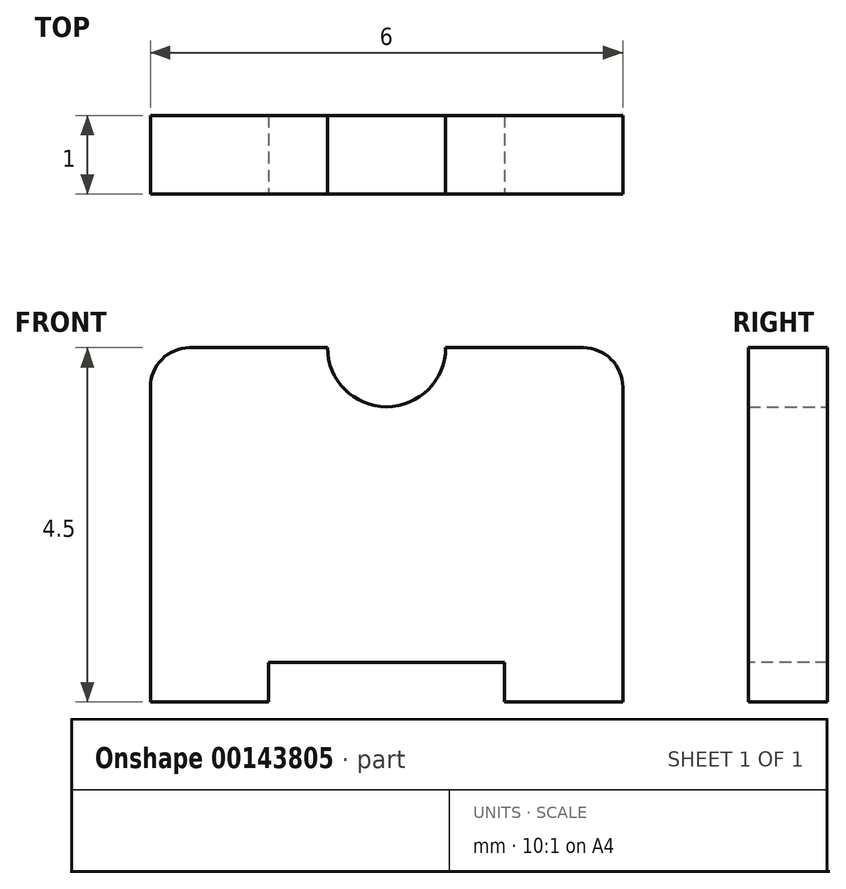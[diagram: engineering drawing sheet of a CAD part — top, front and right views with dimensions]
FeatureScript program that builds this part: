
annotation { "Feature Type Name" : "Feature", "Feature Type Description" : "" }
export const myFeature = defineFeature(function(context is Context, id is Id, definition is map)
    precondition{}
    {
        {
            var Q0;
            Q0=qCreatedBy(makeId("Front.planeOp"),FACE);
            var sketch = newSketch(context, id + "F0", { "sketchPlane" : qUnion([Q0])});
            skArc(sketch, "E0", {"start": v(-0.75, 0) * mm, "mid": v(0, -0.75) * mm, "end": v(0.75, 0) * mm});
            skLineSegment(sketch, "E1", {"start": v(-0.75, 0) * mm, "end": v(-2.5, 0) * mm});
            skLineSegment(sketch, "E2", {"start": v(-3, -0.5) * mm, "end": v(-3, -4.5) * mm});
            skLineSegment(sketch, "E3", {"start": v(-3, -4.5) * mm, "end": v(3, -4.5) * mm});
            skLineSegment(sketch, "E4", {"start": v(3, -4.5) * mm, "end": v(3, -0.5) * mm});
            skLineSegment(sketch, "E5", {"start": v(2.5, 0) * mm, "end": v(0.75, 0) * mm});
            skPoint(sketch, "E6.visualSharp", {"position": v(-3, 0) * mm});
            skArc(sketch, "E6.filletArc", {"start": v(-2.5, 0) * mm, "mid": v(-2.85, -0.15) * mm, "end": v(-3, -0.5) * mm});
            skPoint(sketch, "E7.visualSharp", {"position": v(3, 0) * mm});
            skArc(sketch, "E7.filletArc", {"start": v(3, -0.5) * mm, "mid": v(2.85, -0.15) * mm, "end": v(2.5, 0) * mm});
            skSolve(sketch);
        }
        {
            var Q0;
            Q0 = qSketchRegion(id + "F0", true);
            extrude(context, id + "F1", {"entities" : qUnion([Q0]), "depth" : 1 * mm});
        }
        {
            var Q0;
            Q0=makeQuery(id+"F1.opExtrude","CAP_FACE",FACE,{"disambiguationData":[OSD([sQuery(id+"F0.wireOp",EDGE,"E0"),sQuery(id+"F0.wireOp",EDGE,"E1"),sQuery(id+"F0.wireOp",EDGE,"E2"),sQuery(id+"F0.wireOp",EDGE,"E3"),sQuery(id+"F0.wireOp",EDGE,"E4"),sQuery(id+"F0.wireOp",EDGE,"E5"),sQuery(id+"F0.wireOp",EDGE,"E6.filletArc"),sQuery(id+"F0.wireOp",EDGE,"E7.filletArc")])],"isStart":false});
            var sketch = newSketch(context, id + "F2", { "sketchPlane" : qUnion([Q0])});
            skLineSegment(sketch, "E8", {"start": v(-1.5, -4.5) * mm, "end": v(-1.5, -4) * mm});
            skLineSegment(sketch, "E9", {"start": v(-1.5, -4) * mm, "end": v(1.5, -4) * mm});
            skLineSegment(sketch, "E10", {"start": v(1.5, -4) * mm, "end": v(1.5, -4.5) * mm});
            skSolve(sketch);
        }
        {
            var Q0;
            {var subQ0=sQuery(id+"F2.wireOp",EDGE,"E8");Q0=makeQuery(id+"F2.imprint","IMPRINT",FACE,{"disambiguationData":[TD([[makeQuery(id+"F2.imprint","IMPRINT",EDGE,{"derivedFrom":subQ0}),-1.0]])]});}
            extrude(context, id + "F3", {"entities" : qUnion([Q0]), "operationType" : NewBodyOperationType.REMOVE, "oppositeDirection" : true, "depth" : 25 * mm});
        }
    });
